# Revit family: Pantalla Modelo GL
name_source: partatom
category: Luminarias
units: mm (PartAtom-declared; Revit-internal decimal feet)

## family parameters
Compartido = No
Corte con vacíos al cargar = No
Cota de conector redondo = Diámetro de uso
Origen de luz = No
Punto de cálculo de habitación = No
Se basa en plano de trabajo = Sí
Siempre vertical = No
Tipo de pieza = Normal

## types (2) — shared parameters
Comentarios de vataje = 100-240V
Espesor = 1 mm  [stored 0.00328084 ft]
Fabricante = BRILLANT
Modulo alto = 400 mm  [stored 1.31234 ft]
Modulo largo = 1600 mm  [stored 5.24934 ft]
zero-valued in all types: Elevación por defecto

## per-type parameters (varying)
| type | Descripción | Modelo | Watt per fixture |
| Pantalla Modelo GL_GL30130W.1 | PANTALLA MODELO GL30, PIXEL PITCH 30MM, RESOLUCION DEL PANEL 52X13 DOTS, CANTIDAD POR PANEL DE LED 676 DOTS, CONFIGURACION DE PIXEL 2R1G1B, BRILLO 5000-6000NITS, ACTUALIZACION 16BIT, ESCALA DE GRISES 256 NIVELES, AJUSTE DE BRILLO 1000:1, CONTRASTE 400X1600MM, DIMENSION DEL PANEL 400X1600MM, PANEL 0.64M2, PESO DEL PANEL 10KG, CONSUMO DE ENERGIA 130W, ANGULO DE VISUALIZACION 120/160 GRADOS, DISTANCIA DE VISUALIZACION A 30M, TRANSPARENCIA 63%, PUNTO DE CONTROL <0.0002, DURACION DE LAS LUCES (50% BRILLO) >50,000 HORAS, TEMPERATURA DE OPERACIÓN -30C +40C, HUMEDAD RELATIVA 10%-90%, IP 65, VOLTAJE AC 100-240V/50-60Hz, MODO DE ENTRADA EN CORRIENTE CONSTANTE, SISTEMA OPERATIVO WINDOWS 2000/XP/VISTA/WINDOWS 7, TIPO DE SEÑAL AV/S-VIDEO/VGA/CVBS/HDMI/DVI/SDI, CONTROL DE DISTANCIA HSYV <100M. | GL30130W.1 | 130 |
| Pantalla Modelo GL_GL40150W.1 | PANTALLA MODELO GL40, PIXEL PITCH 40MM, RESOLUCION DEL PANEL 40X10 DOTS, CANTIDAD POR PANEL DE LED 400 DOTS, CONFIGURACION DE PIXEL 3R2G2B, BRILLO 5000-6000NITS, ACTUALIZACION 16BIT, ESCALA DE GRISES 256 NIVELES, AJUSTE DE BRILLO 1000:1, CONTRASTE 400X1600MM, DIMENSION DEL PANEL 400X1600MM, PANEL 0.64M2, PESO DEL PANEL 8KG, CONSUMO DE ENERGIA 150W, ANGULO DE VISUALIZACION 120/160 GRADOS, DISTANCIA DE VISUALIZACION A 40M, TRANSPARENCIA 71%, PUNTO DE CONTROL <0.0002, DURACION DE LAS LUCES (50% BRILLO) >50,000 HORAS, TEMPERATURA DE OPERACIÓN -30C +40C, HUMEDAD RELATIVA 10%-90%, IP 65, VOLTAJE AC 100-240V/50-60Hz, MODO DE ENTRADA EN CORRIENTE CONSTANTE, SISTEMA OPERATIVO WINDOWS 2000/XP/VISTA/WINDOWS 7, TIPO DE SEÑAL AV/S-VIDEO/VGA/CVBS/HDMI/DVI/SDI, CONTROL DE DISTANCIA HSYV <100M. | GL40150W.1 | 150 |

note: [stored X ft] marks values corroborated as IEEE doubles in the binary element streams (Revit-internal decimal feet)

## geometry (parser evidence)
native form markers: Blend x2
no freeform markers — native parametric forms only
